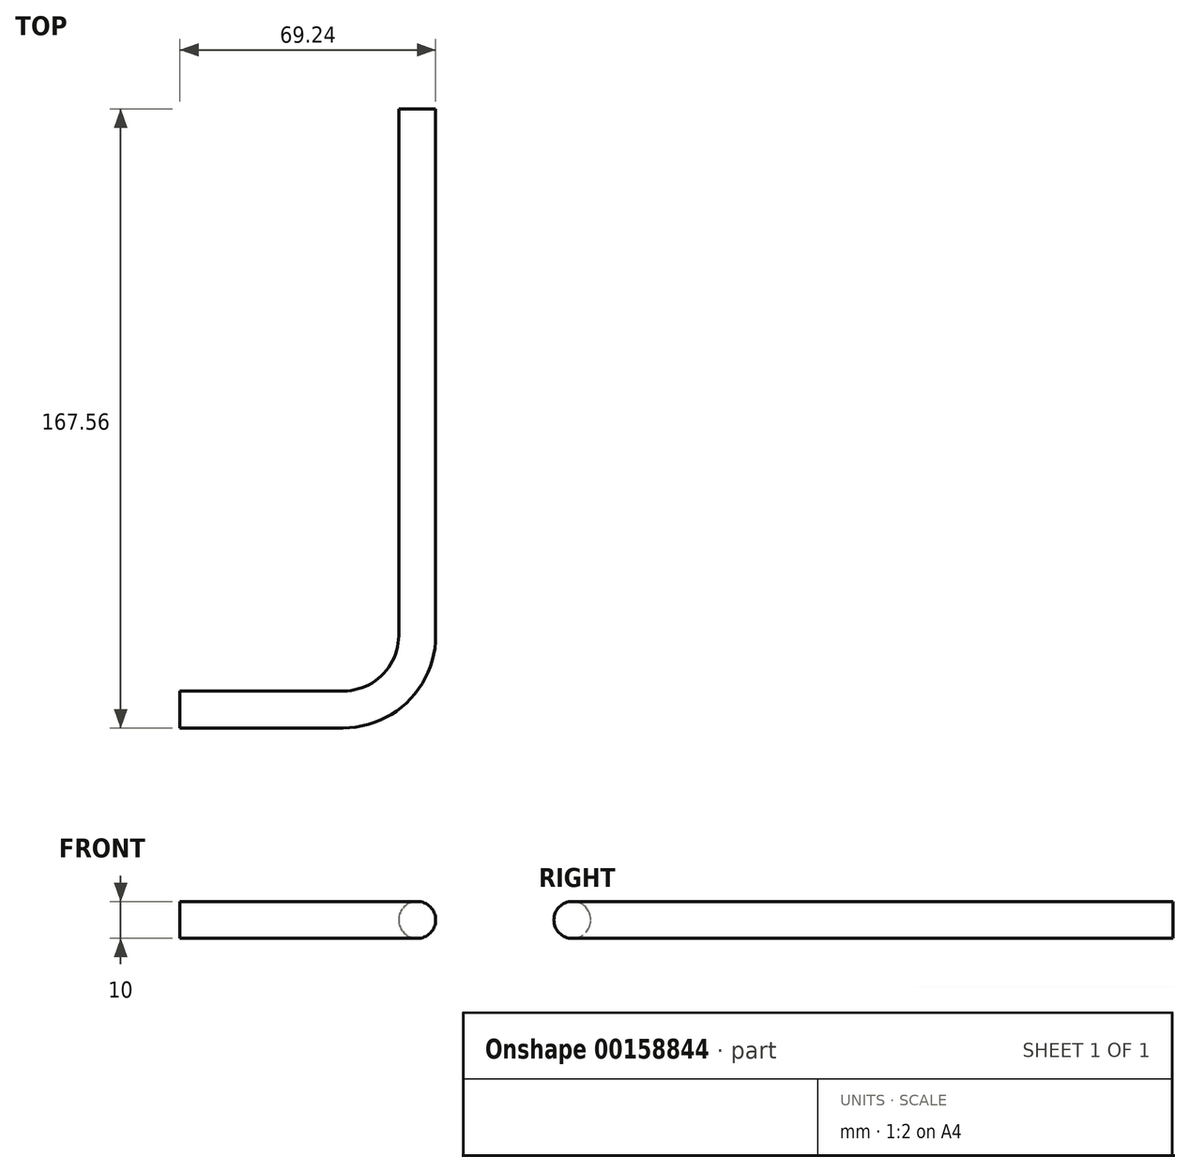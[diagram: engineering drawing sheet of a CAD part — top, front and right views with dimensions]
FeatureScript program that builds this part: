
annotation { "Feature Type Name" : "Feature", "Feature Type Description" : "" }
export const myFeature = defineFeature(function(context is Context, id is Id, definition is map)
    precondition{}
    {
        {
            var Q0;
            Q0=qCreatedBy(makeId("Top.planeOp"),FACE);
            var sketch = newSketch(context, id + "F0", { "sketchPlane" : qUnion([Q0])});
            skLineSegment(sketch, "E0", {"start": v(0, 0) * mm, "end": v(44.23, 0) * mm});
            skLineSegment(sketch, "E1", {"start": v(64.23, 20) * mm, "end": v(64.23, 162.56) * mm});
            skPoint(sketch, "E2.visualSharp", {"position": v(64.23, 0) * mm});
            skArc(sketch, "E2.filletArc", {"start": v(44.23, 0) * mm, "mid": v(58.38, 5.86) * mm, "end": v(64.23, 20) * mm});
            skSolve(sketch);
        }
        {
            var Q0;
            Q0=qCreatedBy(makeId("Right.planeOp"),FACE);
            var sketch = newSketch(context, id + "F1", { "sketchPlane" : qUnion([Q0])});
            skCircle(sketch, "E3", {"center": v(0, 0) * mm, "radius": 5 * mm});
            skSolve(sketch);
        }
        {
            var Q0;
            Q0=makeQuery(id+"F1.imprint","IMPRINT",FACE,{"disambiguationData":[TD([[makeQuery(id+"F1.imprint","IMPRINT",EDGE,{"derivedFrom":sQuery(id+"F1.wireOp",EDGE,"E3")}),1.0]])]});
            var Q1;
            Q1=sQuery(id+"F0.wireOp",EDGE,"E0");
            var Q2;
            Q2=sQuery(id+"F0.wireOp",EDGE,"E1");
            var Q3;
            Q3=sQuery(id+"F0.wireOp",EDGE,"E2.filletArc");
            sweep(context, id + "F2", {"profiles" : qUnion([Q0]), "path" : qUnion([Q1, Q2, Q3])});
        }
    });
